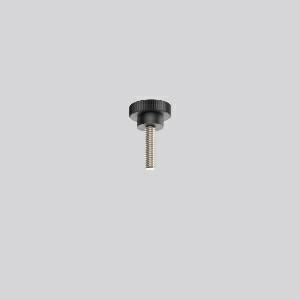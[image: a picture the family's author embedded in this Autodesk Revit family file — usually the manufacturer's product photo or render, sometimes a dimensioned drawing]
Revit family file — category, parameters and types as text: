
# Revit family: linedo_randelschraube_982758_003_ca88
name_source: partatom
category: Lighting Fixtures
units: mm (PartAtom-declared; Revit-internal decimal feet)

## family parameters
Cut with Voids When Loaded = No
Host = Face
Light Source = No
Part Type = Normal
Room Calculation Point = No
Round Connector Dimension = Use Diameter
Shared = No

## types (1)
- LINEDO Rändelschraube
    Apparent Load = 0 VA
    Default Elevation = 1800 mm
    Description = Knurled screw M4 x 15
Colour: black
Diameter: 15 mm
Height: 23 mm
Weight: 3 g
Type of Installation: Surface mounting
    Height = 23 mm
    Lamp = 0 x
    Length = 15 mm
    Luminous efficacy = 0 lm/W
    Manufacturer = RZB
    ModVariant = No
    Model = 982758.003
    Mounting Place = Ceiling
    Mounting Type = Surface mounted
    Number of Poles = 1
    OnlyDefault = Yes
    Power Factor = 1
    Product Name = LINEDO Rändelschraube
    Product group = Surface mounted continuous line luminaire system
    ProductGroupID = 310
    Protection Class = Protection class
    Protection Degree = Degree of protection
    RLX_Detail_Level = 1
    RLX_Emergency_Light_Flux = 0 lm
    RLX_Emergency_Type = 0
    RLX_Emergency_Type_DB = No
    RlxData = <blob elided: 10997 chars, md5=5f9ecb0c>
    Standby Power = 0 W
    System Light Flux = 0 lm
    System Power = 0 W
    Type Comments = Product without accessories
    Type Image = 982758.003.jpg
    URL = http://relux.com
    VarID = ---
    Voltage = 0 V
    Weight = 0.00 kg
    Width = 0 mm  [stored 0 ft]

note: [stored X ft] marks values corroborated as IEEE doubles in the binary element streams (Revit-internal decimal feet)

## geometry (parser evidence)
native form markers: Sweep x8
no freeform markers — native parametric forms only
